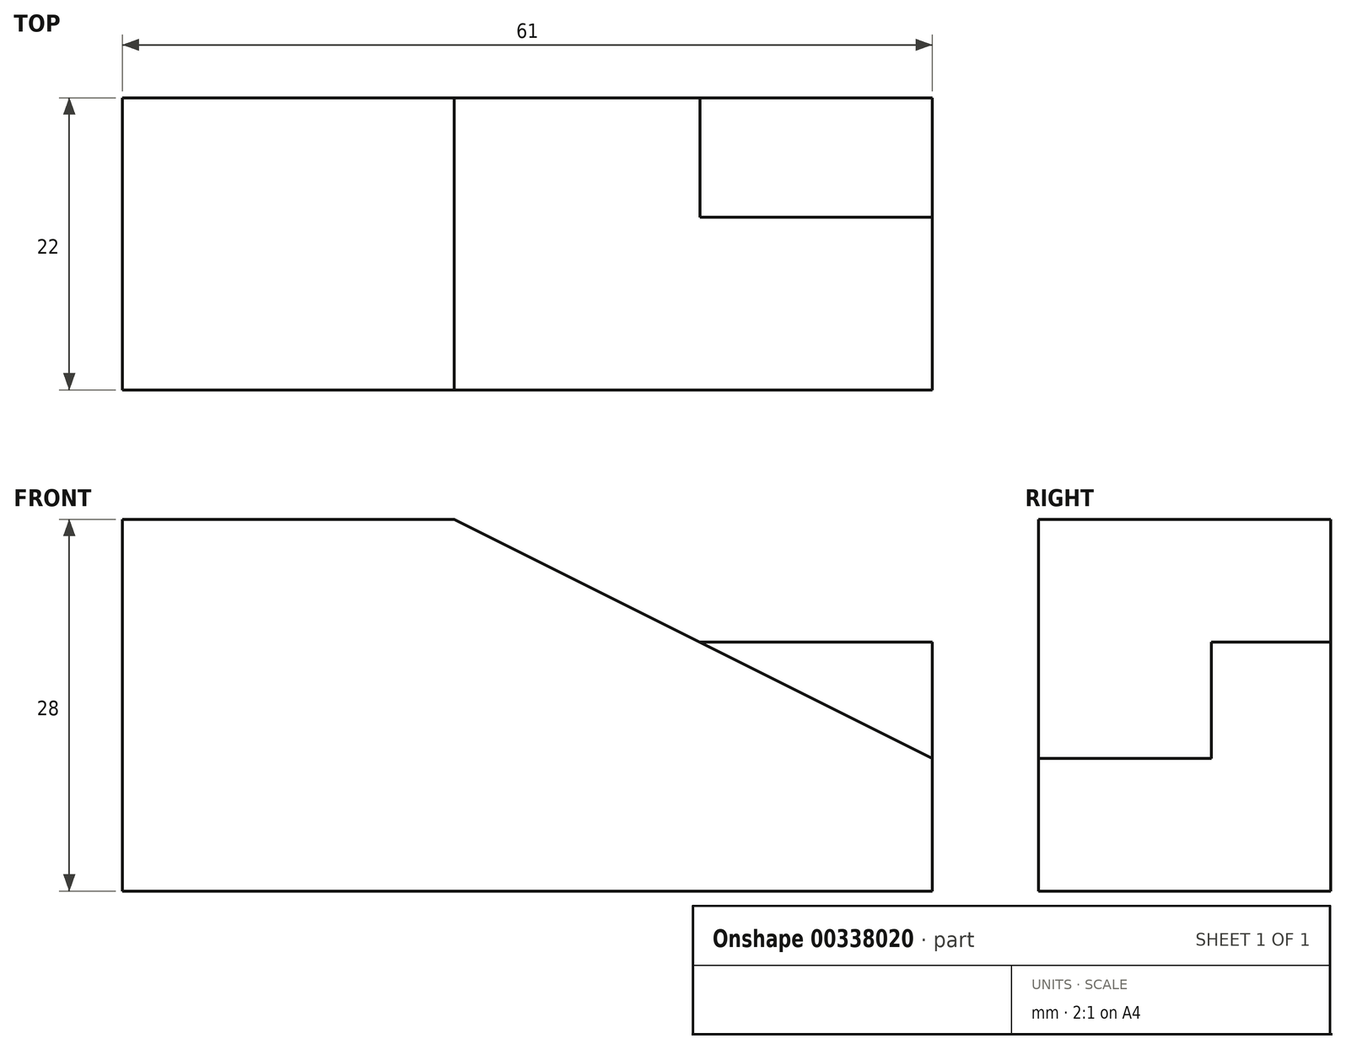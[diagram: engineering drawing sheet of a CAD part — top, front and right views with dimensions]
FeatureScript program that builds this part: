
annotation { "Feature Type Name" : "Feature", "Feature Type Description" : "" }
export const myFeature = defineFeature(function(context is Context, id is Id, definition is map)
    precondition{}
    {
        {
            var Q0;
            Q0=qCreatedBy(makeId("Top.planeOp"),FACE);
            var sketch = newSketch(context, id + "F0", { "sketchPlane" : qUnion([Q0])});
            skLineSegment(sketch, "E0.bottom", {"start": v(0, 0) * mm, "end": v(61, 0) * mm});
            skLineSegment(sketch, "E0.top", {"start": v(0, -22) * mm, "end": v(61, -22) * mm});
            skLineSegment(sketch, "E0.left", {"start": v(0, 0) * mm, "end": v(0, -22) * mm});
            skLineSegment(sketch, "E0.right", {"start": v(61, 0) * mm, "end": v(61, -22) * mm});
            skSolve(sketch);
        }
        {
            var Q0;
            Q0 = qSketchRegion(id + "F0", true);
            extrude(context, id + "F1", {"entities" : qUnion([Q0]), "depth" : 28 * mm});
        }
        {
            var Q0;
            Q0=makeQuery(id+"F1.opExtrude","SWEPT_FACE",FACE,{"disambiguationData":[OSD([sQuery(id+"F0.wireOp",EDGE,"E0.top")])]});
            var sketch = newSketch(context, id + "F2", { "sketchPlane" : qUnion([Q0])});
            skLineSegment(sketch, "E1", {"start": v(61, 28) * mm, "end": v(25, 28) * mm});
            skLineSegment(sketch, "E2", {"start": v(25, 28) * mm, "end": v(61, 10) * mm});
            skLineSegment(sketch, "E3", {"start": v(61, 10) * mm, "end": v(61, 28) * mm});
            skSolve(sketch);
        }
        {
            var Q0;
            Q0 = qSketchRegion(id + "F2", true);
            extrude(context, id + "F3", {"entities" : qUnion([Q0]), "operationType" : NewBodyOperationType.REMOVE, "endBound" : BoundingType.THROUGH_ALL, "oppositeDirection" : true, "depth" : 25 * mm});
        }
        {
            var Q0;
            Q0=makeQuery(id+"F1.opExtrude","SWEPT_FACE",FACE,{"disambiguationData":[OSD([sQuery(id+"F0.wireOp",EDGE,"E0.bottom")])]});
            var sketch = newSketch(context, id + "F4", { "sketchPlane" : qUnion([Q0])});
            skLineSegment(sketch, "E4", {"start": v(-61, 10) * mm, "end": v(-61, 18.75) * mm});
            skLineSegment(sketch, "E5", {"start": v(-61, 18.75) * mm, "end": v(-43.5, 18.75) * mm});
            skLineSegment(sketch, "E6", {"start": v(-43.5, 18.75) * mm, "end": v(-61, 10) * mm});
            skSolve(sketch);
        }
        {
            var Q0;
            Q0 = qSketchRegion(id + "F4", true);
            extrude(context, id + "F5", {"entities" : qUnion([Q0]), "operationType" : NewBodyOperationType.ADD, "oppositeDirection" : true, "depth" : 9 * mm});
        }
    });
